# Revit family: Domotics-DomesticRanges-GEWISS-CHORUS_DATA-SOCKET-OUTLET_TV
name_source: partatom
category: Apparecchi elettrici
revit_build: Autodesk Revit 2016 (Build: 20161004_0715(x64)
units: mm (PartAtom-declared; Revit-internal decimal feet)

## family parameters
Condiviso = Sì
Host = Superficie
Mantenere orientamento annotazione = Sì
Punto di calcolo locali = Sì
Quota connettore circolare = Usa diametro
Taglio con vuoti quando caricato = Sì
Tipo di parte = Normale

## types (12) — shared parameters
Carico apparente = 0 VA
Catalogue = DOMOTICS
Catalogue Range = CHORUS - DOMESTIC RANGE
IDF = 34fc3b6e-676c-4ec9-8993-bd2d13b43123
IDT = 8edb2d1c-7456-4a47-b73a-f2f26e15fbb4
Immagine tipo = GW14361.jpg
N. poli = 1
Produttore = GEWISS S.p.A.
Prospetto di default = 1219 mm
Technical sheet = https://www.gewiss.com
Tipo_ = SYSTEM PRESE TV_GENERICO : GW14361
URL = https://www.gewiss.com
Version file RFA = 19.0
Volt = 230 V

## per-type parameters (varying)
| type | Descrizione | EAN code | Electrocod | Modello |
| GW10362 - TV SOCKET 1M THROUGH 5dB M.CONN 9.5mm W | TV SOCKET 1M THROUGH 5dB M.CONN 9.5mm W | 8011564259577 | 3720 | GW10362 |
| GW14364 - TV SOCKET 1M THROUGH 14dB M.CONN 9.5mm T | TV SOCKET 1M THROUGH 14dB M.CONN 9.5mm T | 8011564266773 | 0131 | GW14364 |
| GW10363 - TV SOCKET 1M THROUGH 10dB M.CONN 9.5mm W | TV SOCKET 1M THROUGH 10dB M.CONN 9.5mm W | 8011564259584 | 0131 | GW10363 |
| GW12363 - TV SOCKET 1M THROUGH 10dB M.CONN 9.5mm B | TV SOCKET 1M THROUGH 10dB M.CONN 9.5mm B | 8011564268913 | 0131 | GW12363 |
| GW12361 - TV SOCKET 1M DIR. MALE CONN. 9.5mm B | TV SOCKET 1M DIR. MALE CONN. 9.5mm B | 8011564266667 | 0131 | GW12361 |
| GW10361 - TV SOCKET 1M DIR. MALE CONN 9.5mm W | TV SOCKET 1M DIR. MALE CONN 9.5mm W | 8011564258969 | 0131 | GW10361 |
| GW12364 - TV SOCKET 1M THROUGH 14dB M.CONN 9.5mm B | TV SOCKET 1M THROUGH 14dB M.CONN 9.5mm B | 8011564268937 | 3720 | GW12364 |
| GW10364 - TV SOCKET 1M THROUGH 14dB M.CONN 9.5mm W | TV SOCKET 1M THROUGH 14dB M.CONN 9.5mm W | 8011564259591 | 0131 | GW10364 |
| GW14363 - TV SOCKET 1M THROUGH 10dB M.CONN 9.5mm T | TV SOCKET 1M THROUGH 10dB M.CONN 9.5mm T | 8011564266766 | 0131 | GW14363 |
| GW14362 - TV SOCKET 1M THROUGH 5dB M.CONN 9.5mm T | TV SOCKET 1M THROUGH 5dB M.CONN 9.5mm T | 8011564266759 | 3721 | GW14362 |
| GW14361 - TV SOCKET 1M DIR. MALE CONN. 9.5mm T | TV SOCKET 1M DIR. MALE CONN. 9.5mm T | 8011564266742 | 0131 | GW14361 |
| GW12362 - TV SOCKET 1M THROUGH 5dB M.CONN 9.5mm B | TV SOCKET 1M THROUGH 5dB M.CONN 9.5mm B | 8011564268906 | 0131 | GW12362 |

## geometry (parser evidence)
native form markers: Sweep x2
no freeform markers — native parametric forms only
